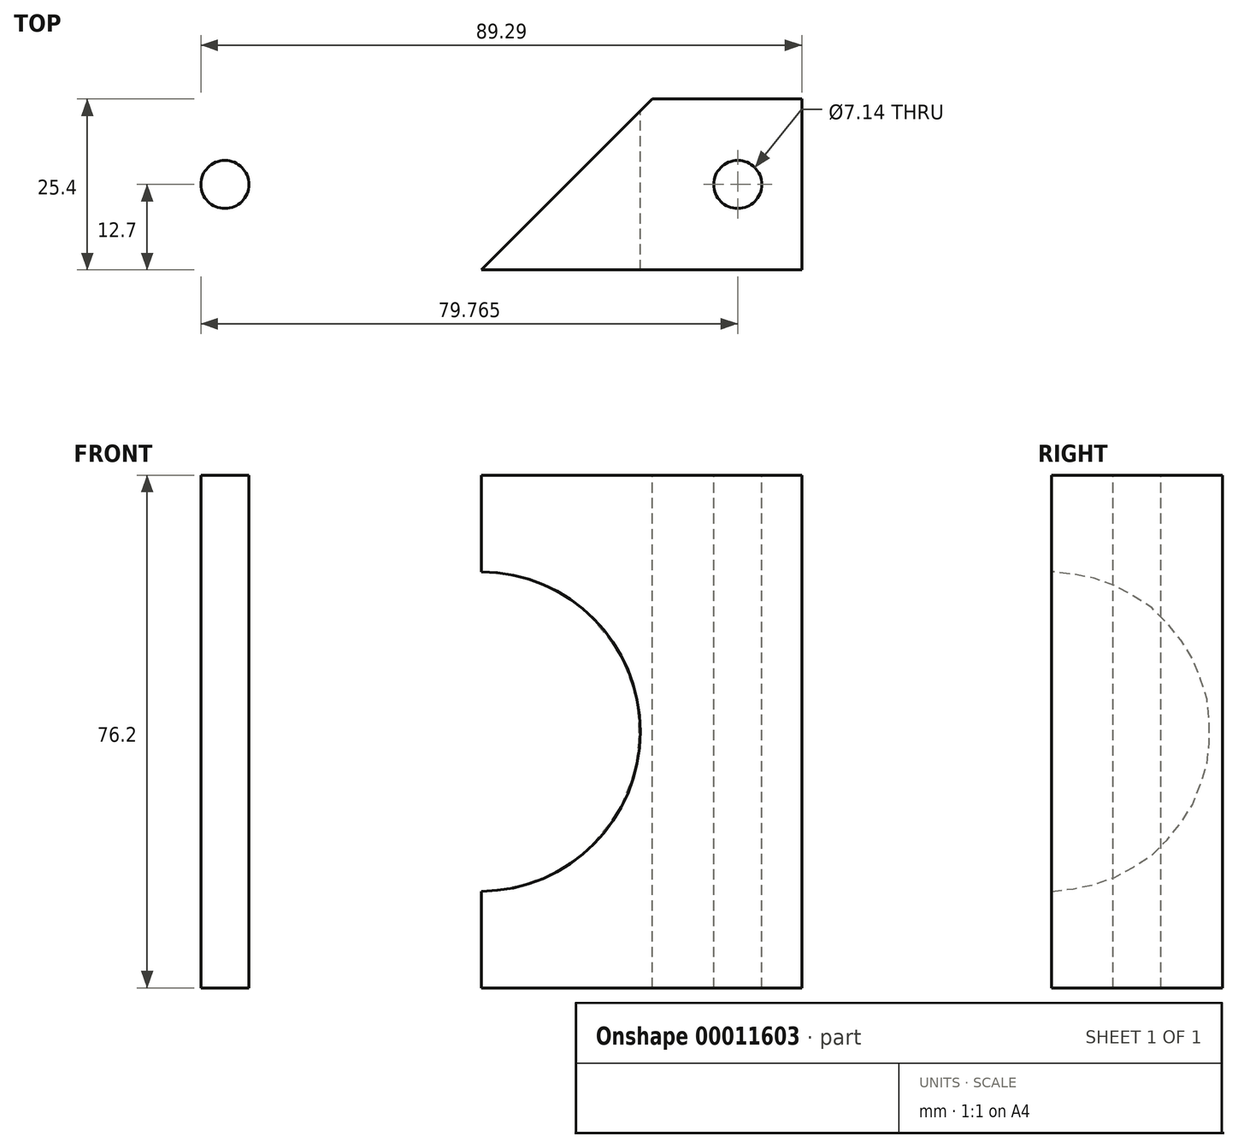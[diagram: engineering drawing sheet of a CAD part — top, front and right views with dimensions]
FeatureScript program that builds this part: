
annotation { "Feature Type Name" : "Feature", "Feature Type Description" : "" }
export const myFeature = defineFeature(function(context is Context, id is Id, definition is map)
    precondition{}
    {
        {
            var Q0;
            Q0=qCreatedBy(makeId("Front.planeOp"),FACE);
            var sketch = newSketch(context, id + "F0", { "sketchPlane" : qUnion([Q0])});
            skLineSegment(sketch, "E0.bottom", {"start": v(0, 0) * mm, "end": v(-95.25, 0) * mm});
            skLineSegment(sketch, "E0.top", {"start": v(0, 76.2) * mm, "end": v(-95.25, 76.2) * mm});
            skLineSegment(sketch, "E0.left", {"start": v(0, 0) * mm, "end": v(0, 76.2) * mm});
            skLineSegment(sketch, "E0.right", {"start": v(-95.25, 0) * mm, "end": v(-95.25, 76.2) * mm});
            skLineSegment(sketch, "E1.0", {"start": v(-47.75, 0) * mm, "end": v(-47.75, 76.2) * mm, "construction": true});
            skCircle(sketch, "E2", {"center": v(-47.75, 38.1) * mm, "radius": 23.75 * mm});
            skSolve(sketch);
        }
        {
            var Q0;
            Q0=makeQuery(id+"F0.imprint","IMPRINT",FACE,{"disambiguationData":[TD([[makeQuery(id+"F0.imprint","IMPRINT",EDGE,{"derivedFrom":sQuery(id+"F0.wireOp",EDGE,"E0.bottom")}),-1.0]])]});
            extrude(context, id + "F1", {"entities" : qUnion([Q0]), "depth" : 25.4 * mm});
        }
        {
            var Q0;
            Q0=makeQuery(id+"F1.opExtrude","SWEPT_FACE",FACE,{"disambiguationData":[OSD([sQuery(id+"F0.wireOp",EDGE,"E0.top")])]});
            var sketch = newSketch(context, id + "F2", { "sketchPlane" : qUnion([Q0])});
            skCircle(sketch, "E3", {"center": v(-9.53, -12.7) * mm, "radius": 3.57 * mm});
            skPoint(sketch, "E4.orphan", {"position": v(-9.53, 0) * mm});
            skPoint(sketch, "E5.0.start.orphan", {"position": v(-9.53, -25.4) * mm});
            skLineSegment(sketch, "E6", {"start": v(-9.53, 0) * mm, "end": v(-9.53, -25.4) * mm, "construction": true});
            skLineSegment(sketch, "E7", {"start": v(-47.63, 0) * mm, "end": v(-47.63, -25.4) * mm, "construction": true});
            skCircle(sketch, "E8.MirrorC", {"center": v(-85.73, -12.7) * mm, "radius": 3.57 * mm});
            skLineSegment(sketch, "E9", {"start": v(-47.63, -25.4) * mm, "end": v(0, 22.23) * mm});
            skSolve(sketch);
        }
        {
            var Q0;
            Q0=makeQuery(id+"F2.imprint","IMPRINT",FACE,{"disambiguationData":[TD([[makeQuery(id+"F2.imprint","IMPRINT",EDGE,{"derivedFrom":sQuery(id+"F2.wireOp",EDGE,"E8.MirrorC")}),-1.0]])]});
            var Q1;
            Q1=makeQuery(id+"F2.imprint","IMPRINT",FACE,{"disambiguationData":[TD([[makeQuery(id+"F2.imprint","IMPRINT",EDGE,{"derivedFrom":sQuery(id+"F2.wireOp",EDGE,"E3")}),1.0]])]});
            extrude(context, id + "F3", {"entities" : qUnion([Q0, Q1]), "operationType" : NewBodyOperationType.REMOVE, "endBound" : BoundingType.THROUGH_ALL, "oppositeDirection" : true, "depth" : 25.4 * mm});
        }
    });
